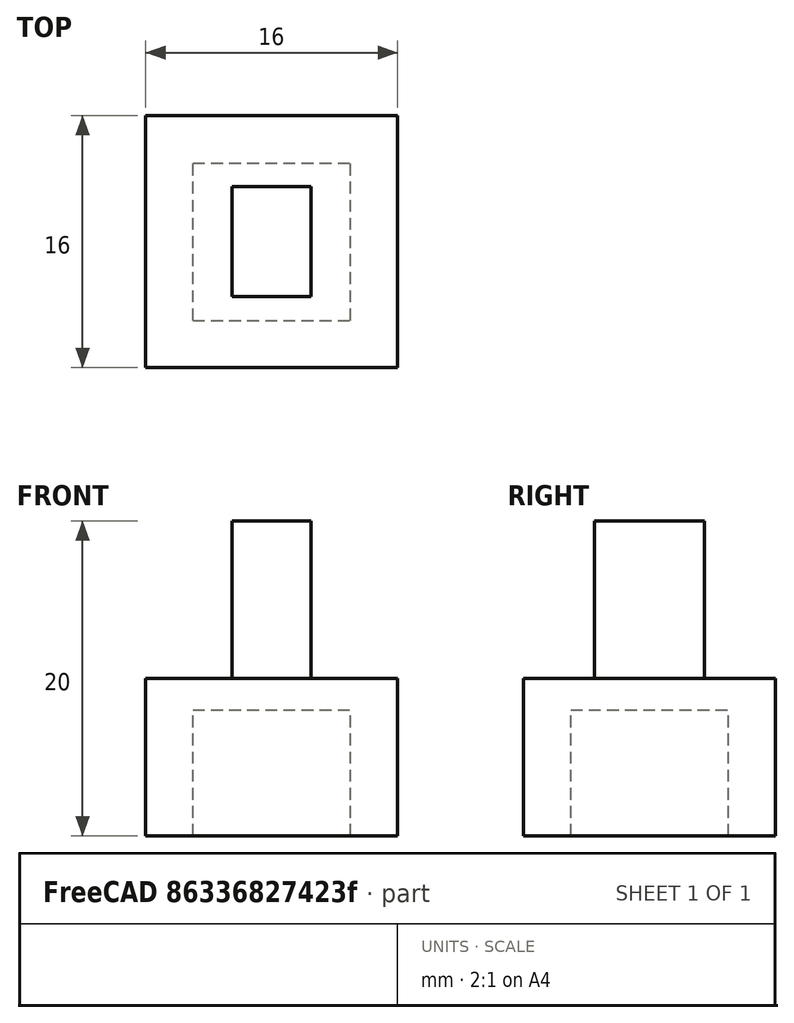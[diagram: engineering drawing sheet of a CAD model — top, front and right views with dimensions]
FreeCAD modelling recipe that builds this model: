
FCSTD DOCUMENT  (FreeCAD 0.18.3R)
Label: prism
License: All rights reserved
LicenseURL: http://en.wikipedia.org/wiki/All_rights_reserved
objects: Part::Box×3, Part::Fuse×1, Part::Cut×1
note: 5 computed .brp shape members not serialized (recipe doc carries the construction recipe); baked Part::Feature solids carry a one-line shape summary decoded from their .brp

FEATURE [Part::Box] Box  label="Cube"
  AttacherType = Attacher::AttachEngine3D
  Height = 10
  Length = 16
  Placement = pos=(-8,-8,0) rot=(0,0,1;0rad)
  Width = 16
FEATURE [Part::Box] Box001  label="Cube001"
  AttacherType = Attacher::AttachEngine3D
  Height = 10
  Length = 5
  Placement = pos=(-2.5,-3.5,10) rot=(0,0,1;0rad)
  Width = 7
FEATURE [Part::Fuse] Fusion
  Base = -> Box
  Tool = -> Box001
FEATURE [Part::Box] Box002  label="Cube002"
  AttacherType = Attacher::AttachEngine3D
  Height = 8
  Length = 10
  Placement = pos=(-5,-5,0) rot=(0,0,1;0rad)
  Width = 10
FEATURE [Part::Cut] Cut
  Base = -> Fusion
  Tool = -> Box002
